# Revit family: ВП_Eng
name_source: partatom
category: Mechanical Equipment
units: mm (PartAtom-declared; Revit-internal decimal feet)

## family parameters
Always vertical = Yes
Classification = None
Cut with Voids When Loaded = No
Part Type = Normal
Room Calculation Point = No
Round Connector Dimension = Use Diameter
Shared = No
Work Plane-Based = No

## types (5) — shared parameters
00_20_Manufacturer = Vents
00_20_Name = Centrifugal ceiling fan
Casing Material = Steel, galvanized
Frequency = 50 Hz
Load Classification = HVAC
Maintenance zone material = <By Category>
Manufacturer = Vents
Number of Fase = 1
URL = https://ventilation-system.com
Voltage = 230 V
zero-valued in all types: Default Elevation

## per-type parameters (varying)
| type | Amperage | Apparent Load | B | B1 | D | Diameter | Dy | H | H1 | Height | L | Length | Lk | Lk1 | Maximum Air Flow | Power | Sound pressure level at 3 m distance | Temperature of moving air | Weight | Width | b | h |
| VP 100 K Q | 0 A | 78 VA | 240 mm  [stored 0.787402 ft] | 200 mm  [stored 0.656168 ft] | 100 mm  [stored 0.328084 ft] | 100 mm  [stored 0.328084 ft] | 95 mm  [stored 0.31168 ft] | 160 mm  [stored 0.524934 ft] | 189 mm  [stored 0.620079 ft] | 189 mm  [stored 0.620079 ft] | 305 mm  [stored 1.00066 ft] | 305 mm  [stored 1.00066 ft] | 300 mm | 0 mm  [stored 0 ft] | 190.0 m³/h | 56 W | 42 dBA | -25...+45 °С | 3.40 kg | 240 mm  [stored 0.787402 ft] | 60 mm  [stored 0.19685 ft] | 80 mm  [stored 0.262467 ft] |
| VP 150 K | 1 A | 115 VA | 355 mm | 315 mm  [stored 1.03346 ft] | 150 mm | 150 mm | 145 mm  [stored 0.475722 ft] | 180 mm  [stored 0.590551 ft] | 215 mm | 215 mm | 419 mm | 419 mm | 90 mm  [stored 0.295276 ft] | 60 mm  [stored 0.19685 ft] | 485.0 m³/h | 112 W | 52 dBA | -25...+50 °С | 6.50 kg | 355 mm | 85 mm  [stored 0.278871 ft] | 90 mm  [stored 0.295276 ft] |
| VP 100 K | 0 A | 60 VA | 240 mm  [stored 0.787402 ft] | 200 mm  [stored 0.656168 ft] | 100 mm  [stored 0.328084 ft] | 100 mm  [stored 0.328084 ft] | 95 mm  [stored 0.31168 ft] | 160 mm  [stored 0.524934 ft] | 189 mm  [stored 0.620079 ft] | 189 mm  [stored 0.620079 ft] | 305 mm  [stored 1.00066 ft] | 305 mm  [stored 1.00066 ft] | 300 mm | 0 mm  [stored 0 ft] | 240.0 m³/h | 61 W | 47 dBA | -25...+50 °С | 3.40 kg | 240 mm  [stored 0.787402 ft] | 60 mm  [stored 0.19685 ft] | 80 mm  [stored 0.262467 ft] |
| VP 125 K Q | 0 A | 78 VA | 240 mm  [stored 0.787402 ft] | 200 mm  [stored 0.656168 ft] | 125 mm  [stored 0.410105 ft] | 125 mm  [stored 0.410105 ft] | 120 mm  [stored 0.393701 ft] | 160 mm  [stored 0.524934 ft] | 189 mm  [stored 0.620079 ft] | 189 mm  [stored 0.620079 ft] | 305 mm  [stored 1.00066 ft] | 305 mm  [stored 1.00066 ft] | 300 mm | 0 mm  [stored 0 ft] | 225.0 m³/h | 56 W | 43 dBA | -25...+45 °С | 3.40 kg | 240 mm  [stored 0.787402 ft] | 73 mm | 80 mm  [stored 0.262467 ft] |
| VP 125 K | 0 A | 60 VA | 240 mm  [stored 0.787402 ft] | 200 mm  [stored 0.656168 ft] | 125 mm  [stored 0.410105 ft] | 125 mm  [stored 0.410105 ft] | 120 mm  [stored 0.393701 ft] | 160 mm  [stored 0.524934 ft] | 189 mm  [stored 0.620079 ft] | 189 mm  [stored 0.620079 ft] | 305 mm  [stored 1.00066 ft] | 305 mm  [stored 1.00066 ft] | 300 mm | 0 mm  [stored 0 ft] | 310.0 m³/h | 61 W | 48 dBA | -25...+50 °С | 3.40 kg | 240 mm  [stored 0.787402 ft] | 73 mm | 80 mm  [stored 0.262467 ft] |

note: column(s) folded — value = type name in every type: 00_20_Type

note: [stored X ft] marks values corroborated as IEEE doubles in the binary element streams (Revit-internal decimal feet)
